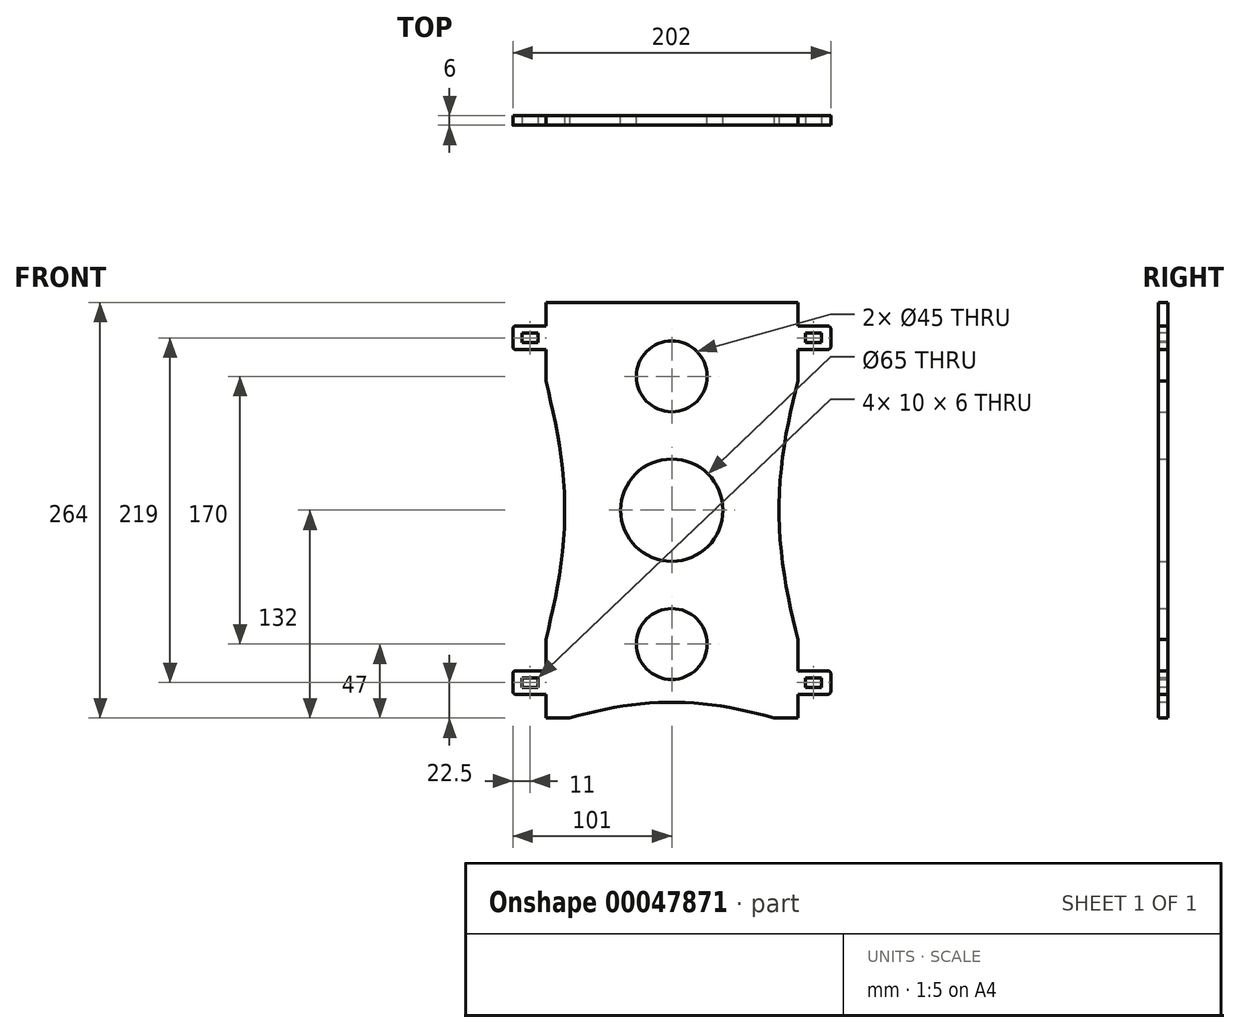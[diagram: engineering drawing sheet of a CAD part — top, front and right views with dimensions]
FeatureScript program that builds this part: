
annotation { "Feature Type Name" : "Feature", "Feature Type Description" : "" }
export const myFeature = defineFeature(function(context is Context, id is Id, definition is map)
    precondition{}
    {
        {
            var Q0;
            Q0=qCreatedBy(makeId("Front.planeOp"),FACE);
            var sketch = newSketch(context, id + "F0", { "sketchPlane" : qUnion([Q0])});
            skLineSegment(sketch, "E0.rect.bottom", {"start": v(-80, 132) * mm, "end": v(80, 132) * mm});
            skLineSegment(sketch, "E0.rect.left", {"start": v(-80, 132) * mm, "end": v(-80, 74.33) * mm});
            skLineSegment(sketch, "E0.rect.right", {"start": v(80, 132) * mm, "end": v(80, -74.33) * mm});
            skLineSegment(sketch, "E1", {"start": v(-80, 117) * mm, "end": v(80, 117) * mm, "construction": true});
            skLineSegment(sketch, "E2.bottom", {"start": v(80, 117) * mm, "end": v(99, 117) * mm});
            skLineSegment(sketch, "E2.top", {"start": v(80, 102) * mm, "end": v(99, 102) * mm});
            skLineSegment(sketch, "E2.left", {"start": v(80, 117) * mm, "end": v(80, 102) * mm});
            skLineSegment(sketch, "E2.right", {"start": v(101, 115) * mm, "end": v(101, 104) * mm});
            skLineSegment(sketch, "E3.MirrorCS", {"start": v(-80, 102) * mm, "end": v(-99, 102) * mm});
            skLineSegment(sketch, "E4.MirrorCS", {"start": v(-101, 115) * mm, "end": v(-101, 104) * mm});
            skLineSegment(sketch, "E5.MirrorCS", {"start": v(-80, 117) * mm, "end": v(-99, 117) * mm});
            skLineSegment(sketch, "E6.MirrorCS", {"start": v(80, -102) * mm, "end": v(99, -102) * mm});
            skLineSegment(sketch, "E7.MirrorCS", {"start": v(101, -115) * mm, "end": v(101, -104) * mm});
            skLineSegment(sketch, "E8.MirrorCS", {"start": v(80, -117) * mm, "end": v(99, -117) * mm});
            skLineSegment(sketch, "E9.MirrorCS", {"start": v(-80, -102) * mm, "end": v(-99, -102) * mm});
            skLineSegment(sketch, "E10.MirrorCS", {"start": v(-101, -115) * mm, "end": v(-101, -104) * mm});
            skLineSegment(sketch, "E11.MirrorCS", {"start": v(-80, -117) * mm, "end": v(-99, -117) * mm});
            skLineSegment(sketch, "E12.trimOffspring", {"start": v(-80, 74.33) * mm, "end": v(-80, -132) * mm});
            skLineSegment(sketch, "E13.trimOffspring", {"start": v(80, -74.33) * mm, "end": v(80, -132) * mm});
            skLineSegment(sketch, "E14.trimOffspring", {"start": v(-80, -132) * mm, "end": v(80, -132) * mm});
            skPoint(sketch, "E15.visualSharp", {"position": v(-101, 117) * mm});
            skArc(sketch, "E15.filletArc", {"start": v(-99, 117) * mm, "mid": v(-100.41, 116.41) * mm, "end": v(-101, 115) * mm});
            skPoint(sketch, "E16.visualSharp", {"position": v(-101, 102) * mm});
            skArc(sketch, "E16.filletArc", {"start": v(-101, 104) * mm, "mid": v(-100.41, 102.59) * mm, "end": v(-99, 102) * mm});
            skPoint(sketch, "E17.visualSharp", {"position": v(101, 117) * mm});
            skArc(sketch, "E17.filletArc", {"start": v(101, 115) * mm, "mid": v(100.41, 116.41) * mm, "end": v(99, 117) * mm});
            skPoint(sketch, "E18.visualSharp", {"position": v(101, 102) * mm});
            skArc(sketch, "E18.filletArc", {"start": v(99, 102) * mm, "mid": v(100.41, 102.59) * mm, "end": v(101, 104) * mm});
            skPoint(sketch, "E19.visualSharp", {"position": v(101, -102) * mm});
            skArc(sketch, "E19.filletArc", {"start": v(101, -104) * mm, "mid": v(100.41, -102.59) * mm, "end": v(99, -102) * mm});
            skPoint(sketch, "E20.visualSharp", {"position": v(101, -117) * mm});
            skArc(sketch, "E20.filletArc", {"start": v(99, -117) * mm, "mid": v(100.41, -116.41) * mm, "end": v(101, -115) * mm});
            skPoint(sketch, "E21.visualSharp", {"position": v(-101, -102) * mm});
            skArc(sketch, "E21.filletArc", {"start": v(-99, -102) * mm, "mid": v(-100.41, -102.59) * mm, "end": v(-101, -104) * mm});
            skPoint(sketch, "E22.visualSharp", {"position": v(-101, -117) * mm});
            skArc(sketch, "E22.filletArc", {"start": v(-101, -115) * mm, "mid": v(-100.41, -116.41) * mm, "end": v(-99, -117) * mm});
            skCircle(sketch, "E23", {"center": v(0, 0) * mm, "radius": 32.5 * mm});
            skCircle(sketch, "E24", {"center": v(0, 85) * mm, "radius": 22.5 * mm});
            skCircle(sketch, "E25.MirrorC", {"center": v(0, -85) * mm, "radius": 22.5 * mm});
            skSolve(sketch);
        }
        {
            var Q0;
            Q0=qSketchRegion(id+"F0",true);
            extrude(context, id + "F1", {"entities" : qUnion([Q0]), "depth" : 6 * mm});
        }
        {
            var Q0;
            Q0=makeQuery(id+"F1.opExtrude","CAP_FACE",FACE,{"disambiguationData":[OSD([sQuery(id+"F0.wireOp",EDGE,"E0.rect.bottom"),sQuery(id+"F0.wireOp",EDGE,"E0.rect.top"),sQuery(id+"F0.wireOp",EDGE,"E0.rect.left"),sQuery(id+"F0.wireOp",EDGE,"E0.rect.right"),sQuery(id+"F0.wireOp",EDGE,"E2.bottom"),sQuery(id+"F0.wireOp",EDGE,"E2.top"),sQuery(id+"F0.wireOp",EDGE,"E2.right"),sQuery(id+"F0.wireOp",EDGE,"E3.MirrorCS"),sQuery(id+"F0.wireOp",EDGE,"E4.MirrorCS"),sQuery(id+"F0.wireOp",EDGE,"E5.MirrorCS"),sQuery(id+"F0.wireOp",EDGE,"E6.MirrorCS"),sQuery(id+"F0.wireOp",EDGE,"E7.MirrorCS"),sQuery(id+"F0.wireOp",EDGE,"E8.MirrorCS"),sQuery(id+"F0.wireOp",EDGE,"E9.MirrorCS"),sQuery(id+"F0.wireOp",EDGE,"E10.MirrorCS"),sQuery(id+"F0.wireOp",EDGE,"E11.MirrorCS"),sQuery(id+"F0.wireOp",EDGE,"af97b2eb-19e3-4ed1-a5cc-9d5d14b4319e"),sQuery(id+"F0.wireOp",EDGE,"fd276fa8-d1b3-416b-b574-707db09a5048"),sQuery(id+"F0.wireOp",EDGE,"6cabffeb-77b6-4d30-9aa5-3118ea41b9000.MirrorC"),sQuery(id+"F0.wireOp",EDGE,"E12.trimOffspring"),sQuery(id+"F0.wireOp",EDGE,"E13.trimOffspring"),sQuery(id+"F0.wireOp",EDGE,"E14.trimOffspring"),sQuery(id+"F0.wireOp",EDGE,"E15.filletArc"),sQuery(id+"F0.wireOp",EDGE,"E16.filletArc"),sQuery(id+"F0.wireOp",EDGE,"E17.filletArc"),sQuery(id+"F0.wireOp",EDGE,"E18.filletArc"),sQuery(id+"F0.wireOp",EDGE,"E19.filletArc"),sQuery(id+"F0.wireOp",EDGE,"E20.filletArc"),sQuery(id+"F0.wireOp",EDGE,"E21.filletArc"),sQuery(id+"F0.wireOp",EDGE,"E22.filletArc"),sQuery(id+"F0.wireOp",EDGE,"54247ffd-c9f2-4c1b-9410-b82cb3885be3.filletArc"),sQuery(id+"F0.wireOp",EDGE,"112347d6-ac97-47eb-8ed1-f6758d2802ee.filletArc"),sQuery(id+"F0.wireOp",EDGE,"f3a4c7c8-d4c1-4512-80d6-b9807c804e30.filletArc"),sQuery(id+"F0.wireOp",EDGE,"b78cc7f0-be37-44b0-885f-f8ae3ed7ed6b.filletArc"),sQuery(id+"F0.wireOp",EDGE,"c977bad6-1547-4923-ac52-0fdde740afa2.filletArc"),sQuery(id+"F0.wireOp",EDGE,"793bfdfc-7d73-47e8-a734-bd20596823b7.filletArc")])],"isStart":false});
            var sketch = newSketch(context, id + "F2", { "sketchPlane" : qUnion([Q0])});
            skLineSegment(sketch, "E26.bottom", {"start": v(-95, 112.5) * mm, "end": v(-85, 112.5) * mm});
            skLineSegment(sketch, "E26.top", {"start": v(-95, 106.5) * mm, "end": v(-85, 106.5) * mm});
            skLineSegment(sketch, "E26.left", {"start": v(-95, 112.5) * mm, "end": v(-95, 106.5) * mm});
            skLineSegment(sketch, "E26.right", {"start": v(-85, 112.5) * mm, "end": v(-85, 106.5) * mm});
            skLineSegment(sketch, "E27", {"start": v(-80, 117) * mm, "end": v(-80, 102) * mm, "construction": true});
            skLineSegment(sketch, "E28", {"start": v(-80, 109.5) * mm, "end": v(-98.66, 109.5) * mm, "construction": true});
            skPoint(sketch, "E29", {"position": v(-85, 109.5) * mm});
            skLineSegment(sketch, "E30.MirrorCS", {"start": v(95, 112.5) * mm, "end": v(85, 112.5) * mm});
            skLineSegment(sketch, "E31.MirrorCS", {"start": v(95, 112.5) * mm, "end": v(95, 106.5) * mm});
            skLineSegment(sketch, "E32.MirrorCS", {"start": v(95, 106.5) * mm, "end": v(85, 106.5) * mm});
            skLineSegment(sketch, "E33.MirrorCS", {"start": v(85, 112.5) * mm, "end": v(85, 106.5) * mm});
            skLineSegment(sketch, "E34.MirrorCS", {"start": v(-95, -106.5) * mm, "end": v(-85, -106.5) * mm});
            skLineSegment(sketch, "E35.MirrorCS", {"start": v(-95, -112.5) * mm, "end": v(-95, -106.5) * mm});
            skLineSegment(sketch, "E36.MirrorCS", {"start": v(-95, -112.5) * mm, "end": v(-85, -112.5) * mm});
            skLineSegment(sketch, "E37.MirrorCS", {"start": v(-85, -112.5) * mm, "end": v(-85, -106.5) * mm});
            skLineSegment(sketch, "E38.MirrorCS", {"start": v(95, -112.5) * mm, "end": v(85, -112.5) * mm});
            skLineSegment(sketch, "E39.MirrorCS", {"start": v(85, -112.5) * mm, "end": v(85, -106.5) * mm});
            skLineSegment(sketch, "E40.MirrorCS", {"start": v(95, -106.5) * mm, "end": v(85, -106.5) * mm});
            skLineSegment(sketch, "E41.MirrorCS", {"start": v(95, -112.5) * mm, "end": v(95, -106.5) * mm});
            skSolve(sketch);
        }
        {
            var Q0;
            Q0=qSketchRegion(id+"F2",true);
            extrude(context, id + "F3", {"entities" : qUnion([Q0]), "operationType" : NewBodyOperationType.REMOVE, "oppositeDirection" : true, "depth" : 25 * mm});
        }
        {
            var Q0;
            Q0=makeQuery(id+"F1.opExtrude","CAP_FACE",FACE,{"disambiguationData":[OSD([sQuery(id+"F0.wireOp",EDGE,"E0.rect.bottom"),sQuery(id+"F0.wireOp",EDGE,"E0.rect.left"),sQuery(id+"F0.wireOp",EDGE,"E0.rect.right"),sQuery(id+"F0.wireOp",EDGE,"E2.bottom"),sQuery(id+"F0.wireOp",EDGE,"E2.top"),sQuery(id+"F0.wireOp",EDGE,"E2.right"),sQuery(id+"F0.wireOp",EDGE,"E3.MirrorCS"),sQuery(id+"F0.wireOp",EDGE,"E4.MirrorCS"),sQuery(id+"F0.wireOp",EDGE,"E5.MirrorCS"),sQuery(id+"F0.wireOp",EDGE,"E6.MirrorCS"),sQuery(id+"F0.wireOp",EDGE,"E7.MirrorCS"),sQuery(id+"F0.wireOp",EDGE,"E8.MirrorCS"),sQuery(id+"F0.wireOp",EDGE,"E9.MirrorCS"),sQuery(id+"F0.wireOp",EDGE,"E10.MirrorCS"),sQuery(id+"F0.wireOp",EDGE,"E11.MirrorCS"),sQuery(id+"F0.wireOp",EDGE,"E12.trimOffspring"),sQuery(id+"F0.wireOp",EDGE,"E13.trimOffspring"),sQuery(id+"F0.wireOp",EDGE,"E14.trimOffspring"),sQuery(id+"F0.wireOp",EDGE,"E15.filletArc"),sQuery(id+"F0.wireOp",EDGE,"E16.filletArc"),sQuery(id+"F0.wireOp",EDGE,"E17.filletArc"),sQuery(id+"F0.wireOp",EDGE,"E18.filletArc"),sQuery(id+"F0.wireOp",EDGE,"E19.filletArc"),sQuery(id+"F0.wireOp",EDGE,"E20.filletArc"),sQuery(id+"F0.wireOp",EDGE,"E21.filletArc"),sQuery(id+"F0.wireOp",EDGE,"E22.filletArc"),sQuery(id+"F0.wireOp",EDGE,"E23"),sQuery(id+"F0.wireOp",EDGE,"E24"),sQuery(id+"F0.wireOp",EDGE,"E25.MirrorC")])],"isStart":false});
            var sketch = newSketch(context, id + "F4", { "sketchPlane" : qUnion([Q0])});
            skLineSegment(sketch, "E42", {"start": v(0, -132) * mm, "end": v(0, -122) * mm, "construction": true});
            skLineSegment(sketch, "E43", {"start": v(-65, -132) * mm, "end": v(-65, -149.14) * mm});
            skLineSegment(sketch, "E44.MirrorCS", {"start": v(65, -132) * mm, "end": v(65, -149.14) * mm});
            skFitSpline(sketch, "E45", {"points": [v(-65, -132) * mm, v(0, -122) * mm, v(65, -132) * mm], "startDerivative": vector(130, 36.97) * mm, "endDerivative": vector(130, -36.97) * mm});
            skLineSegment(sketch, "E46", {"start": v(-65, -149.14) * mm, "end": v(65, -149.14) * mm});
            skLineSegment(sketch, "E47", {"start": v(80, 0) * mm, "end": v(68, 0) * mm, "construction": true});
            skPoint(sketch, "E47.endSnap0", {"position": v(80, 0) * mm});
            skLineSegment(sketch, "E48", {"start": v(80, 82) * mm, "end": v(104.24, 82) * mm});
            skLineSegment(sketch, "E49.MirrorCS", {"start": v(80, -82) * mm, "end": v(104.24, -82) * mm});
            skFitSpline(sketch, "E50", {"points": [v(80, 82) * mm, v(68, 0) * mm, v(80, -82) * mm], "startDerivative": vector(-36, -144) * mm, "endDerivative": vector(36, -144) * mm});
            skLineSegment(sketch, "E51", {"start": v(104.24, 82) * mm, "end": v(104.24, -82) * mm});
            skFitSpline(sketch, "E52.MirrorCS", {"points": [v(-80, 82) * mm, v(-68, 0) * mm, v(-80, -82) * mm], "startDerivative": vector(36, -144) * mm, "endDerivative": vector(-36, -144) * mm});
            skLineSegment(sketch, "E53.MirrorCS", {"start": v(-80, 82) * mm, "end": v(-104.24, 82) * mm});
            skLineSegment(sketch, "E54.MirrorCS", {"start": v(-104.24, 82) * mm, "end": v(-104.24, -82) * mm});
            skLineSegment(sketch, "E55.MirrorCS", {"start": v(-80, -82) * mm, "end": v(-104.24, -82) * mm});
            skSolve(sketch);
        }
        {
            var Q0;
            Q0 = qSketchRegion(id + "F4", true);
            extrude(context, id + "F5", {"entities" : qUnion([Q0]), "operationType" : NewBodyOperationType.REMOVE, "oppositeDirection" : true, "depth" : 25 * mm});
        }
    });
